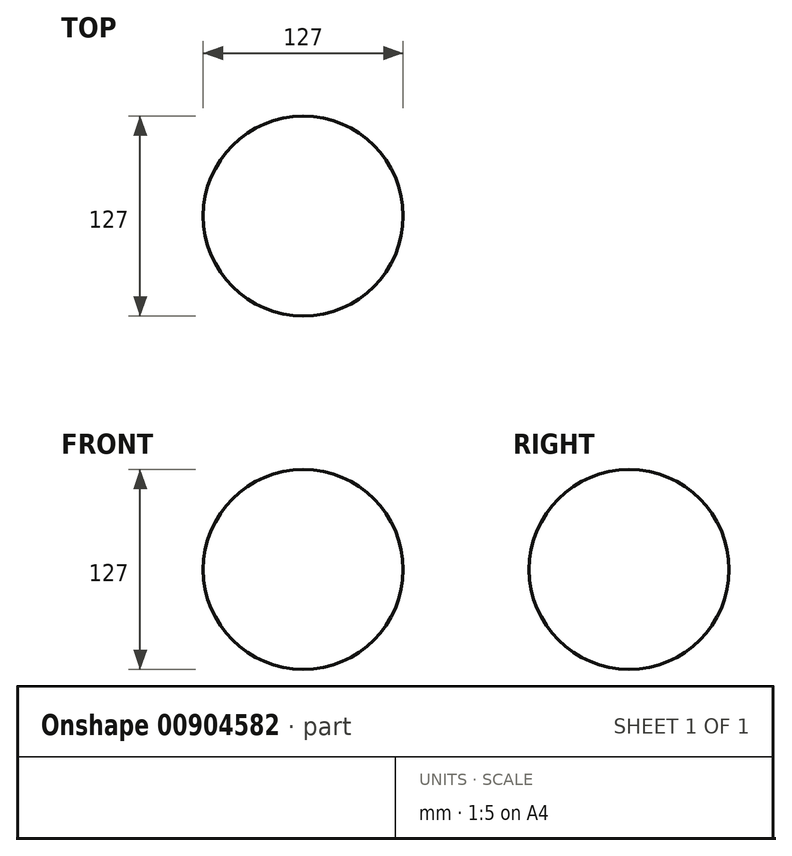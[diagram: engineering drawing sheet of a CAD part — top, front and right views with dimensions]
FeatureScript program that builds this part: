
annotation { "Feature Type Name" : "Feature", "Feature Type Description" : "" }
export const myFeature = defineFeature(function(context is Context, id is Id, definition is map)
    precondition{}
    {
        {
            var Q0;
            Q0=qCreatedBy(makeId("Front.planeOp"),FACE);
            var sketch = newSketch(context, id + "F0", { "sketchPlane" : qUnion([Q0])});
            skLineSegment(sketch, "E0", {"start": v(-63.5, 0) * mm, "end": v(63.5, 0) * mm});
            skArc(sketch, "E1", {"start": v(-63.5, 0) * mm, "mid": v(0, -63.5) * mm, "end": v(63.5, 0) * mm});
            skSolve(sketch);
        }
        {
            var Q0;
            Q0 = qSketchRegion(id + "F0", true);
            var Q1;
            Q1=sQuery(id+"F0.wireOp",EDGE,"E0");
            revolve(context, id + "F1", {"surfaceOperationType" : NewSurfaceOperationType.NEW, "entities" : qUnion([Q0]), "axis" : qUnion([Q1]), "revolveType" : RevolveType.FULL});
        }
        {
            var Q0;
            Q0=qCreatedBy(makeId("Top.planeOp"),FACE);
            cPlane(context, id + "F2", {"entities" : qUnion([Q0]), "cplaneType" : CPlaneType.OFFSET, "offset" : 101.6 * mm, "width" : 152.4 * mm, "height" : 152.4 * mm});
        }
    });
